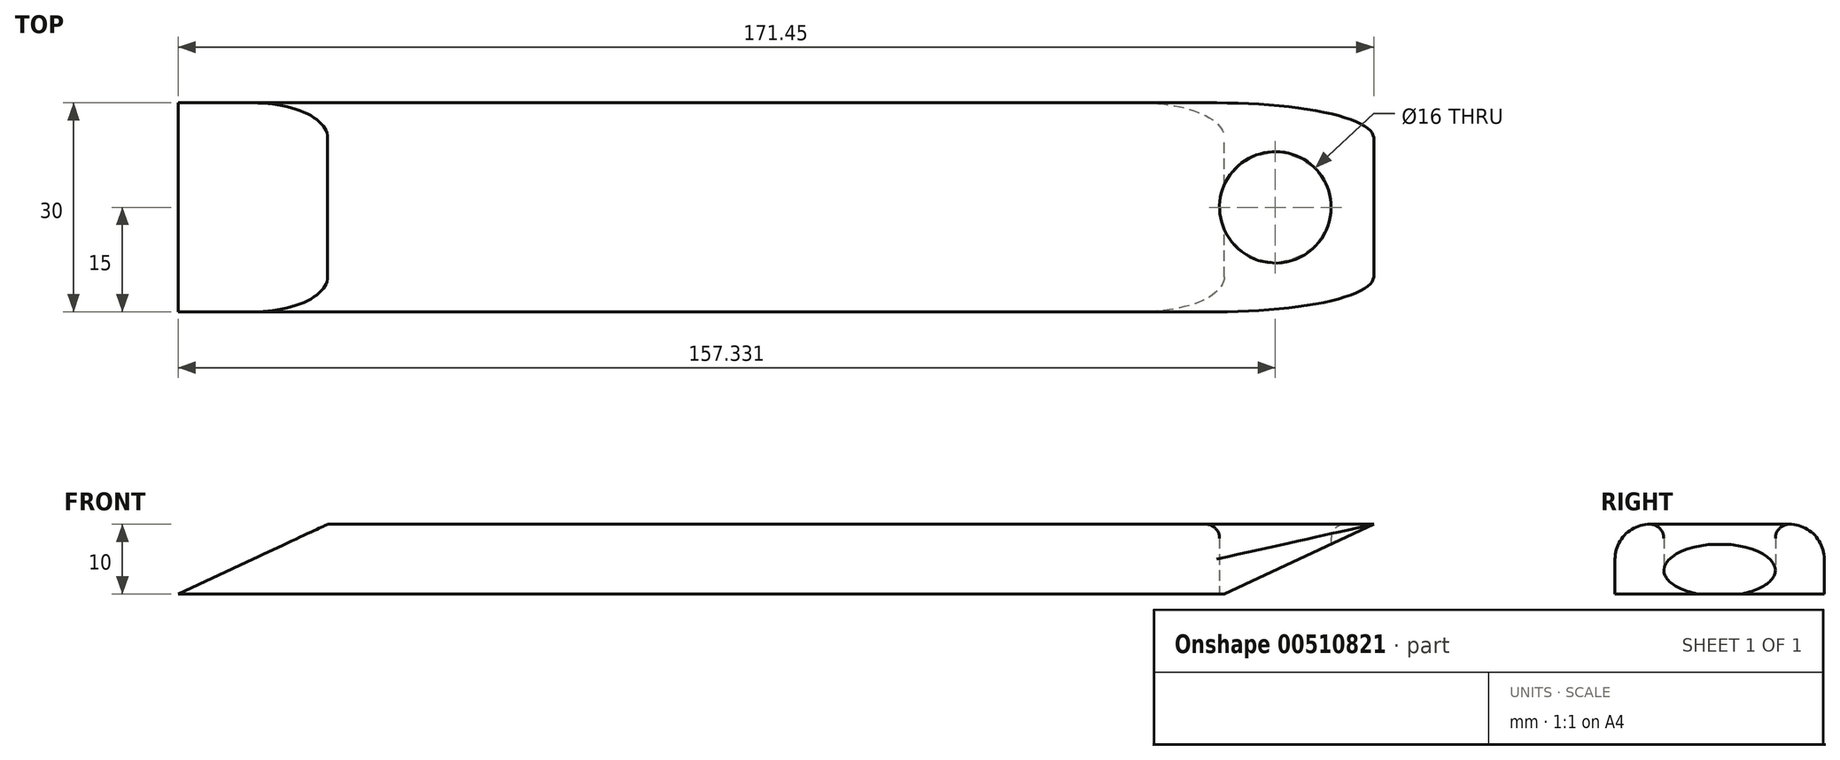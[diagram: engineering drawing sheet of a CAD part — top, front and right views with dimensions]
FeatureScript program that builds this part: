
annotation { "Feature Type Name" : "Feature", "Feature Type Description" : "" }
export const myFeature = defineFeature(function(context is Context, id is Id, definition is map)
    precondition{}
    {
        {
            var Q0;
            Q0=qCreatedBy(makeId("Front.planeOp"),FACE);
            var sketch = newSketch(context, id + "F0", { "sketchPlane" : qUnion([Q0])});
            skLineSegment(sketch, "E0", {"start": v(-66.05, 0) * mm, "end": v(-44.6, 10) * mm});
            skLineSegment(sketch, "E1", {"start": v(-44.6, 10) * mm, "end": v(105.4, 10) * mm});
            skLineSegment(sketch, "E2", {"start": v(105.4, 10) * mm, "end": v(83.95, 0) * mm});
            skLineSegment(sketch, "E3", {"start": v(83.95, 0) * mm, "end": v(-66.05, 0) * mm});
            skSolve(sketch);
        }
        {
            var Q0;
            Q0 = qSketchRegion(id + "F0", true);
            extrude(context, id + "F1", {"entities" : qUnion([Q0]), "depth" : 30 * mm});
        }
        {
            var Q0;
            Q0=qCreatedBy(makeId("Top.planeOp"),FACE);
            var sketch = newSketch(context, id + "F2", { "sketchPlane" : qUnion([Q0])});
            skPoint(sketch, "E4.0", {"position": v(30.4, -5) * mm});
            skPoint(sketch, "E5.0", {"position": v(30.4, -25) * mm});
            skLineSegment(sketch, "E6", {"start": v(30.4, -5) * mm, "end": v(30.4, -25) * mm, "construction": true});
            skPoint(sketch, "E7.0", {"position": v(105.4, -15) * mm});
            skLineSegment(sketch, "E8", {"start": v(105.4, -15) * mm, "end": v(30.4, -15) * mm, "construction": true});
            skCircle(sketch, "E9", {"center": v(91.28, -15) * mm, "radius": 8 * mm});
            skSolve(sketch);
        }
        {
            var Q0;
            Q0 = qSketchRegion(id + "F2", true);
            extrude(context, id + "F3", {"entities" : qUnion([Q0]), "operationType" : NewBodyOperationType.REMOVE, "depth" : 25 * mm, "offsetDistance" : 25 * mm});
        }
        {
            var Q0;
            Q0=makeQuery(id+"F1.opExtrude","CAP_EDGE",EDGE,{"disambiguationData":[OSD([sQuery(id+"F0.wireOp",EDGE,"E1")])],"isStart":true});
            var Q1;
            Q1=makeQuery(id+"F1.opExtrude","CAP_EDGE",EDGE,{"disambiguationData":[OSD([sQuery(id+"F0.wireOp",EDGE,"E1")])],"isStart":false});
            var Q2;
            Q2=makeQuery(id+"F1.opExtrude","CAP_EDGE",EDGE,{"disambiguationData":[OSD([sQuery(id+"F0.wireOp",EDGE,"E2")])],"isStart":false});
            var Q3;
            Q3=makeQuery(id+"F1.opExtrude","CAP_EDGE",EDGE,{"disambiguationData":[OSD([sQuery(id+"F0.wireOp",EDGE,"E2")])],"isStart":true});
            fillet(context, id + "F4", {"entities" : qUnion([Q0, Q1, Q2, Q3]), "radius" : 5 * mm, "tangentPropagation" : true, "allowEdgeOverflow" : false});
        }
        {
            var Q0;
            Q0=makeQuery(id+"F3.boolean.opBoolean","INTERSECT",EDGE,{"derivedFrom":[makeQuery(id+"F1.opExtrude","SWEPT_FACE",FACE,{"disambiguationData":[OSD([sQuery(id+"F0.wireOp",EDGE,"E1")])]}),makeQuery(id+"F3.opExtrude","SWEPT_FACE",FACE,{"disambiguationData":[OSD([sQuery(id+"F2.wireOp",EDGE,"E9")])]})]});
            fillet(context, id + "F5", {"entities" : qUnion([Q0]), "radius" : 2 * mm, "tangentPropagation" : true, "allowEdgeOverflow" : false});
        }
    });
